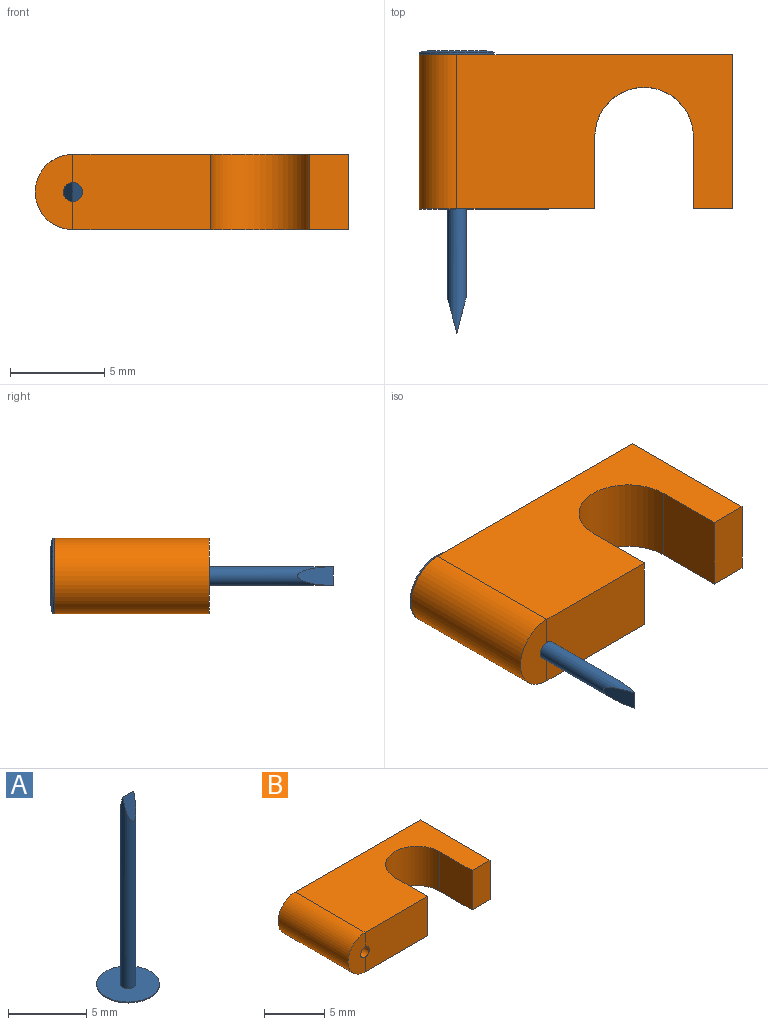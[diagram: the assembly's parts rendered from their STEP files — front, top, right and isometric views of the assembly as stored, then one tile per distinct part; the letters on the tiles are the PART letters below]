
ASSEMBLY  parts=2 mates=1
PART A: 8 faces, bbox 4.9x4.9x15 mm
  f0: cylinder r=0.5mm len=14.83mm, axis (0,0,-1), area 42.8mm2, adj f1,f3,f6,f7
  f1: plane 1x0.01mm, normal (0,0,1), area 0mm2, adj f0,f6,f7
  f2: cylinder r=2mm len=4mm, axis (0,0,-1), area 0.9mm2, adj f3,f5
  f3: plane 4x4mm, normal (0,0,1), area 11.8mm2, adj f0,f2
  f4: plane 3.13x3.13mm, normal (0,0,-1), area 7.7mm2, adj f5
  f5: torus R=1.56mm, axis (0,0,-1), area 5.1mm2, adj f2,f4
  f6: plane 1.93x1mm, normal (0,0.97,0.25), area 1.6mm2, adj f0,f1
  f7: plane 1.88x1mm, normal (0,-0.97,0.26), area 1.5mm2, adj f0,f1
PART B: 12 faces, bbox 16.7x8.2x4 mm
  f0: plane 7.35x4.01mm, normal (0,-1,0), area 28.9mm2, adj f1,f2,f8,f9,f11
  f1: plane 4.01x2.01mm, normal (0,-1,0), area 5.9mm2, adj f0,f10,f11
  f2: plane 4x3.84mm, normal (1,0,0), area 15.4mm2, adj f0,f3,f8,f9
  f3: cylinder r=2.62mm len=5.24mm, axis (0,0,-1), area 32.9mm2, adj f2,f4,f8,f9
  f4: plane 4x3.84mm, normal (-1,0,0), area 15.4mm2, adj f3,f5,f8,f9
  f5: plane 4x2.1mm, normal (0,-1,0), area 8.4mm2, adj f4,f6,f8,f9
  f6: plane 8.21x4mm, normal (1,0,0), area 32.8mm2, adj f5,f7,f8,f9
  f7: plane 16.67x4mm, normal (0,1,0), area 64.2mm2, adj f6,f8,f9,f10,f11
  f8: plane 14.67x8.21mm, normal (0,0,1), area 89.5mm2, adj f0,f2,f3,f4,f5,f6,f7,f10
  f9: plane 14.67x8.21mm, normal (0,0,-1), area 89.5mm2, adj f0,f2,f3,f4,f5,f6,f7,f10
  f10: cylinder r=2mm len=8.21mm, axis (0,1,0), area 51.6mm2, adj f1,f7,f8,f9
  f11: cylinder r=0.5mm len=8.21mm, axis (0,-1,0), area 25.8mm2, adj f0,f1,f7
PLACE A rot(axis=(0.58,0.58,-0.58),120deg) t=(8.99,9.09,9.78)mm
PLACE B t=(8.99,0.69,7.78)mm
MATE slider A.f0 <-> B.f10  axis (0,1,0) through (8.99,1.5,9.78)mm
